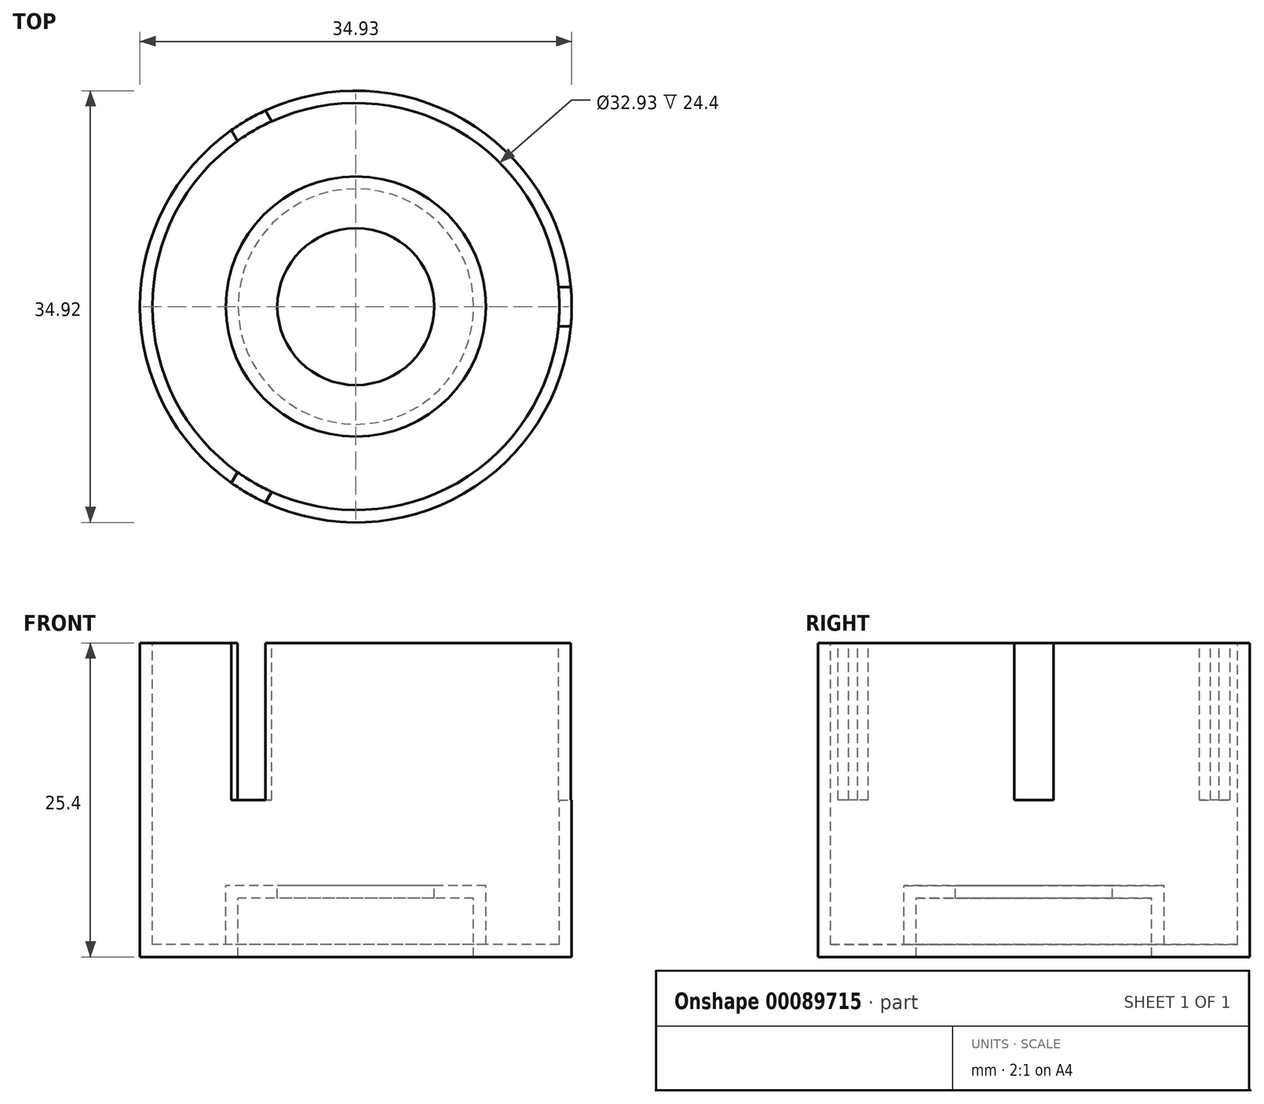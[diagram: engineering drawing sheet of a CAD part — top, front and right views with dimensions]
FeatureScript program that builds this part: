
annotation { "Feature Type Name" : "Feature", "Feature Type Description" : "" }
export const myFeature = defineFeature(function(context is Context, id is Id, definition is map)
    precondition{}
    {
        {
            var Q0;
            Q0=qCreatedBy(makeId("Front.planeOp"),FACE);
            var sketch = newSketch(context, id + "F0", { "sketchPlane" : qUnion([Q0])});
            skLineSegment(sketch, "E0", {"start": v(-76.73, 25.4) * mm, "end": v(-76.73, 0) * mm});
            skLineSegment(sketch, "E1", {"start": v(-76.73, 0) * mm, "end": v(-84.67, 0) * mm});
            skLineSegment(sketch, "E2", {"start": v(-84.67, 0) * mm, "end": v(-84.67, 4.76) * mm});
            skLineSegment(sketch, "E3", {"start": v(-84.67, 4.76) * mm, "end": v(-94.2, 4.76) * mm});
            skLineSegment(sketch, "E4.0", {"start": v(-83.67, 5.76) * mm, "end": v(-94.2, 5.76) * mm});
            skLineSegment(sketch, "E4.1", {"start": v(-83.67, 1) * mm, "end": v(-83.67, 5.76) * mm});
            skLineSegment(sketch, "E4.2", {"start": v(-77.73, 1) * mm, "end": v(-83.67, 1) * mm});
            skLineSegment(sketch, "E4.3", {"start": v(-77.73, 25.4) * mm, "end": v(-77.73, 1) * mm});
            skLineSegment(sketch, "E5", {"start": v(-77.73, 25.4) * mm, "end": v(-76.73, 25.4) * mm});
            skLineSegment(sketch, "E6", {"start": v(-94.2, 5.76) * mm, "end": v(-94.2, 4.76) * mm});
            skLineSegment(sketch, "E7.bottom", {"start": v(-87.85, 2.98) * mm, "end": v(-100.55, 2.98) * mm});
            skLineSegment(sketch, "E7.top", {"start": v(-87.85, 8.54) * mm, "end": v(-100.55, 8.54) * mm});
            skLineSegment(sketch, "E7.left", {"start": v(-87.85, 2.98) * mm, "end": v(-87.85, 8.54) * mm});
            skLineSegment(sketch, "E7.right", {"start": v(-100.55, 2.98) * mm, "end": v(-100.55, 8.54) * mm});
            skPoint(sketch, "E7.middle", {"position": v(-94.2, 5.76) * mm});
            skPoint(sketch, "E8.middle", {"position": v(-77.73, 25.4) * mm});
            skSolve(sketch);
        }
        {
            var Q0;
            Q0=makeQuery(id+"F0.imprint","IMPRINT",FACE,{"disambiguationData":[TD([[makeQuery(id+"F0.imprint","IMPRINT",EDGE,{"derivedFrom":sQuery(id+"F0.wireOp",EDGE,"E0")}),-1.0]])]});
            var Q1;
            {var subQ5=sQuery(id+"F0.wireOp",EDGE,"E1");Q1=makeQuery(id+"F0.imprint","IMPRINT",FACE,{"disambiguationData":[TD([[makeQuery(id+"F0.imprint","IMPRINT",EDGE,{"derivedFrom":subQ5}),-1.0]])]});}
            var Q2;
            Q2=sQuery(id+"F0.wireOp",EDGE,"E6");
            revolve(context, id + "F1", {"entities" : qUnion([Q0, Q1]), "axis" : qUnion([Q2]), "revolveType" : RevolveType.FULL});
        }
        {
            var Q0;
            Q0=sQuery(id+"F0.wireOp",EDGE,"E1");
            var Q1;
            Q1=sQuery(id+"F0.wireOp",VERTEX,"E1.start");
            cPlane(context, id + "F2", {"entities" : qUnion([Q0, Q1]), "cplaneType" : CPlaneType.LINE_POINT, "offset" : 150 * mm, "width" : 150 * mm, "height" : 150 * mm});
        }
        {
            var Q0;
            Q0=qCreatedBy(id+"F2.planeOp",FACE);
            var sketch = newSketch(context, id + "F3", { "sketchPlane" : qUnion([Q0])});
            skLineSegment(sketch, "E9.bottom", {"start": v(-1.59, 12.7) * mm, "end": v(1.59, 12.7) * mm});
            skLineSegment(sketch, "E9.top", {"start": v(-1.59, 25.4) * mm, "end": v(1.59, 25.4) * mm});
            skLineSegment(sketch, "E9.left", {"start": v(-1.59, 12.7) * mm, "end": v(-1.59, 25.4) * mm});
            skLineSegment(sketch, "E9.right", {"start": v(1.59, 12.7) * mm, "end": v(1.59, 25.4) * mm});
            skPoint(sketch, "E9.middle", {"position": v(0, 19.05) * mm});
            skSolve(sketch);
        }
        {
            var Q0;
            Q0=makeQuery(id+"F3.imprint","IMPRINT",FACE,{"disambiguationData":[TD([[makeQuery(id+"F3.imprint","IMPRINT",EDGE,{"derivedFrom":sQuery(id+"F3.wireOp",EDGE,"E9.bottom")}),1.0]])]});
            extrude(context, id + "F4", {"entities" : qUnion([Q0]), "endBound" : BoundingType.SYMMETRIC, "depth" : 10 * mm});
        }
        {
            var Q0;
            Q0=makeQuery(id+"F4.opExtrude","SWEPT_BODY",BODY,{"disambiguationData":[OSD([sQuery(id+"F3.wireOp",EDGE,"E9.bottom"),sQuery(id+"F3.wireOp",EDGE,"E9.top"),sQuery(id+"F3.wireOp",EDGE,"E9.left"),sQuery(id+"F3.wireOp",EDGE,"E9.right")])]});
            var Q1;
            Q1=sQuery(id+"F0.wireOp",EDGE,"E6");
            circularPattern(context, id + "F5", {"operationType" : NewBodyOperationType.REMOVE, "entities" : qUnion([Q0]), "axis" : qUnion([Q1]), "angle" : 120 * degree, "instanceCount" : 3});
        }
    });
